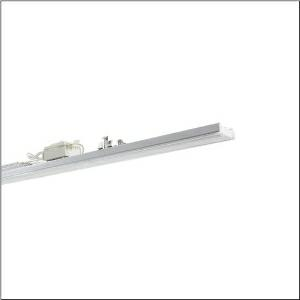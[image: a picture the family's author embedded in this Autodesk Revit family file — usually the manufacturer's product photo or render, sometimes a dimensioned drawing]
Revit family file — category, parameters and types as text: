
# Revit family: licross_11_recessed_mo_51tl12dn4axg3s
name_source: partatom
category: Lighting Fixtures
units: mm (PartAtom-declared; Revit-internal decimal feet)

## family parameters
Cut with Voids When Loaded = No
Host = Face
Light Source = No
Part Type = Normal
Room Calculation Point = No
Round Connector Dimension = Use Diameter
Shared = No

## types (1)
- --- (1 x LED, 1010 lm, 6.7 W, 4000K)
    Apparent Load = 7 VA
    CIE Flux Codes = 67 92 99 100 100
    Color Rendering = 80
    Color Temperature = 4000K
    Default Elevation = 1800 mm
    Description = Licross 11 Recessed MO, luminaire insert, of sheet steel, coil coated, white, length: 1.500mm, width: 66mm, height: 67mm, LED rated luminous flux: 10.240lm, light colour: 840, SDCM (Standard Deviation of Colour Matching)MacAdam ≤ 2 SDCM (initial), control gear: DALI 2 (for two DALI lines), with plug, 6-pole, with phase selection, for trunking rail, 14-core, mains connection: 220..240V, AC, 50/60Hz, rated input power: 61W, for trunking rail, 14-core, internal wiring halogen-free, for emergency light function, converter,control gear: single battery element, battery: LiFePO4, 9Ah, primary optical cover: cover, of PMMA, light emission: direct distribution, primary light characteristic: symmetric, protection rating (complete): IP40, insulation class (complete): insulation class I (protective earthing), certification: CE, UKCA, protection symbol: D if used in an environment without relevant dust loads with corresponding accessories, impact resistance: IK06, permissible ambient temperature for indoor applications: +5..+35°C, standard: EN 60598-2-22, LABS conformity tested according to VDMA 24364:2018-05, reducing of maximum allowable ambient temperature of 5°C with ceiling mounting, corresponds to IFS (International Featured Standards) requirements for safety and quality in the food industry, The light source and the operating device comply with the requirements of the Ecodesign Regulation (EU) 2019/2020 and are replaceable in accordance with this regulation, packaging unit: 1 piece
    Height = 58 mm
    Lamp = 1 x LED
    Lamp Light Flux = 1010 lm
    Lamp Power = 6.7 W
    Lamp count = 1
    Length = 1500 mm
    Luminous efficacy = 151 lm/W
    Manufacturer = Siteco
    ModVariant = No
    Model = 51TL12DN4AXG3S
    Mounting Place = Ceiling
    Mounting Type = Pendant
    Number of Poles = 1
    OnlyDefault = Yes
    Power Factor = 1
    Product Name = Licross 11 Recessed MO
    Product group = luminaire insert | ceiling pendant
    ProductGroupID = 901
    Protection Class = Protection class I
    Protection Degree = IP 40
    RLX_Detail_Level = 1
    RLX_Emergency_Light_Flux = 0 lm
    RLX_Emergency_Type = 0
    RLX_Emergency_Type_DB = No
    RlxData = <blob elided: 25077 chars, md5=f7480988>
    Socket = socket
    Standby Power = 0 W
    System Light Flux = 1010 lm
    System Power = 7 W
    Type Comments = : emergency light operation: 3 h
    Type Image = l_1296930.jpg
    URL = http://relux.com
    VarID = @adj_094193
    Voltage = 0 V
    Weight = 0.00 kg
    Width = 66 mm

## geometry (parser evidence)
native form markers: Blend x4, Sweep x11
no freeform markers — native parametric forms only
